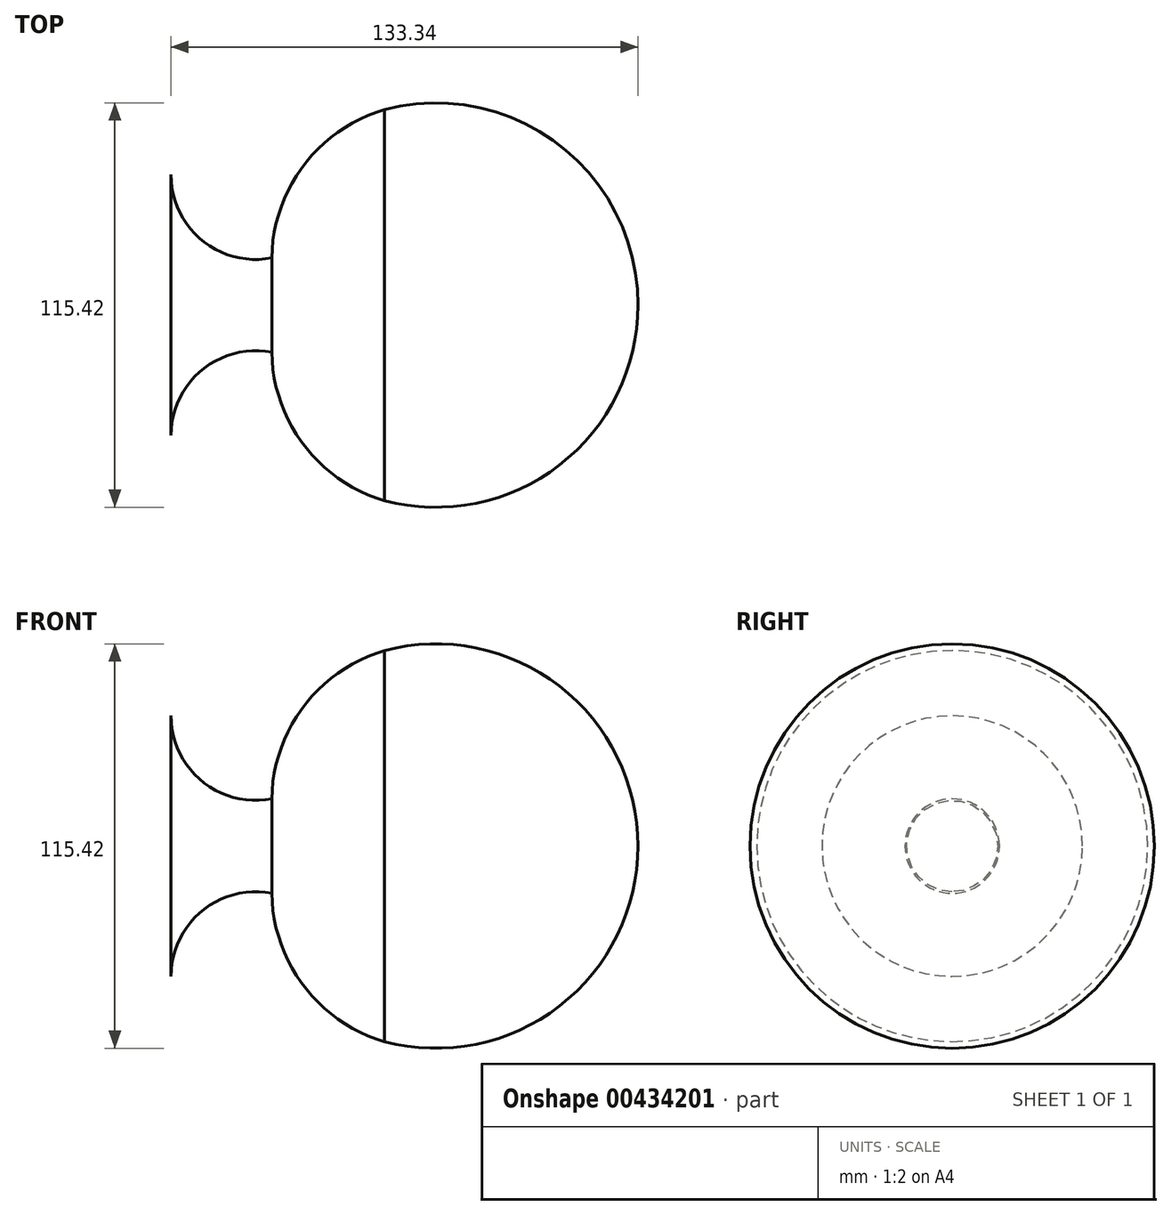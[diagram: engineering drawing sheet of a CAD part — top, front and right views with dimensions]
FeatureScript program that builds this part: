
annotation { "Feature Type Name" : "Feature", "Feature Type Description" : "" }
export const myFeature = defineFeature(function(context is Context, id is Id, definition is map)
    precondition{}
    {
        {
            var Q0;
            Q0=qCreatedBy(makeId("Top.planeOp"),FACE);
            var sketch = newSketch(context, id + "F0", { "sketchPlane" : qUnion([Q0])});
            skLineSegment(sketch, "E0", {"start": v(0, 0) * mm, "end": v(0, 37.19) * mm});
            skArc(sketch, "E1", {"start": v(0, 37.19) * mm, "mid": v(8.8, 18.54) * mm, "end": v(28.78, 13.48) * mm});
            skArc(sketch, "E2", {"start": v(60.95, 55.81) * mm, "mid": v(37.9, 39.94) * mm, "end": v(28.78, 13.48) * mm});
            skArc(sketch, "E3", {"start": v(133.34, 0) * mm, "mid": v(110.87, 45.7) * mm, "end": v(60.95, 55.81) * mm});
            skLineSegment(sketch, "E4", {"start": v(133.34, 0) * mm, "end": v(133.34, -43.9) * mm, "construction": true});
            skLineSegment(sketch, "E5", {"start": v(0, 0) * mm, "end": v(229.13, 0) * mm, "construction": true});
            skSolve(sketch);
        }
        {
            var Q0;
            Q0 = qSketchRegion(id + "F0", true);
            var Q1;
            Q1 = qConstructionFilter(qBodyType(qCreatedBy(id + "F0" ,EDGE), BodyType.WIRE), ConstructionObject.NO);
            var Q2;
            Q2=sQuery(id+"F0.wireOp",EDGE,"E5");
            revolve(context, id + "F1", {"bodyType" : ToolBodyType.SURFACE, "entities" : qUnion([Q0]), "surfaceEntities" : qUnion([Q1]), "axis" : qUnion([Q2]), "revolveType" : RevolveType.FULL});
        }
    });
